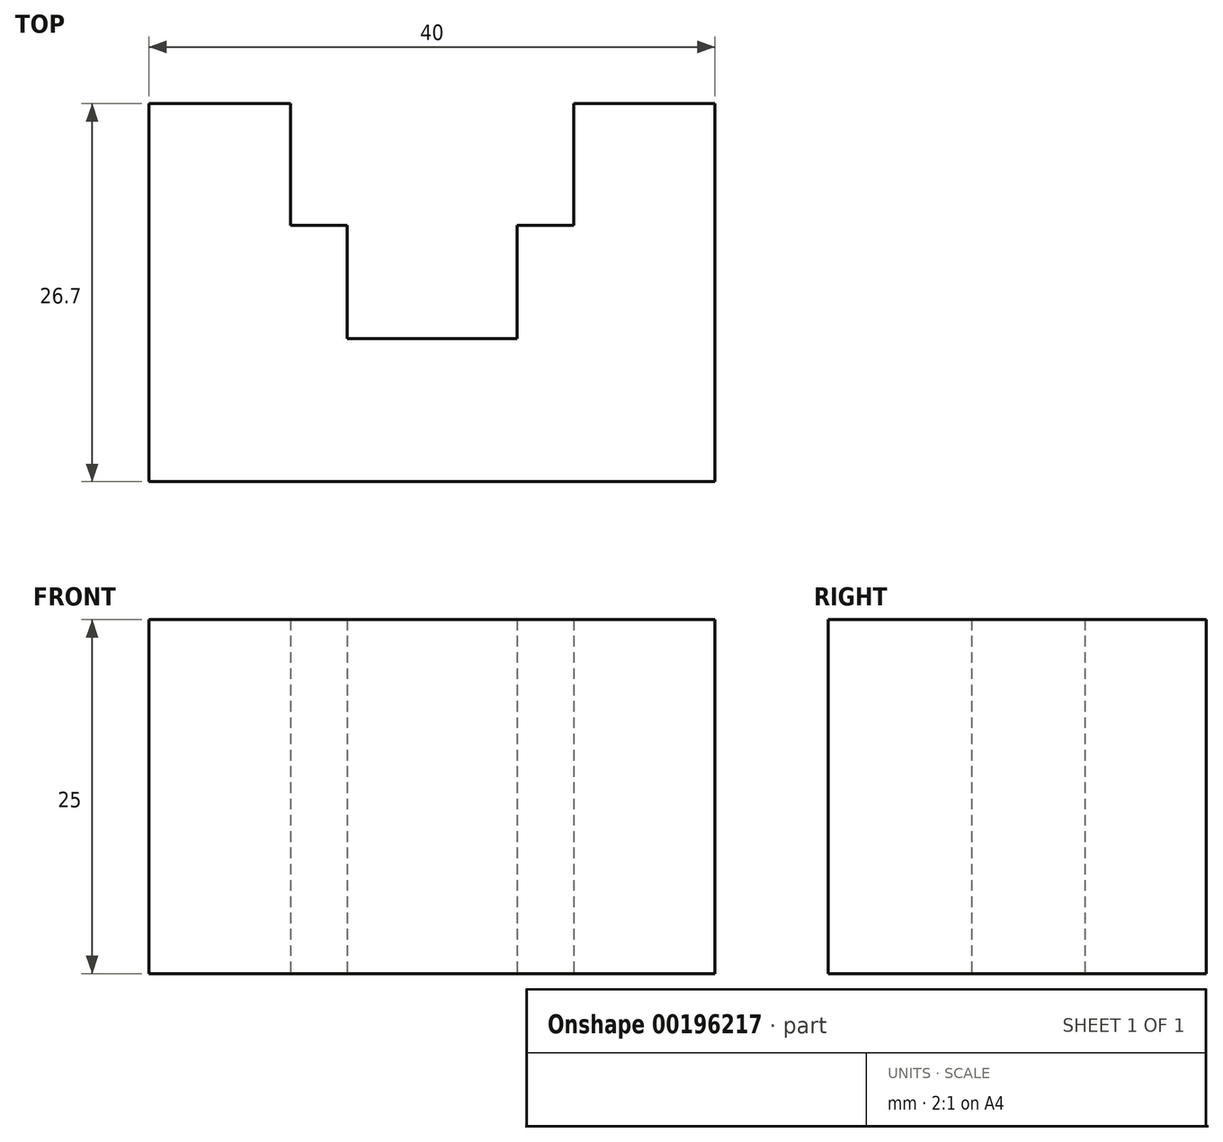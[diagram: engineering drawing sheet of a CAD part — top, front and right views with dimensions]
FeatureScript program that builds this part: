
annotation { "Feature Type Name" : "Feature", "Feature Type Description" : "" }
export const myFeature = defineFeature(function(context is Context, id is Id, definition is map)
    precondition{}
    {
        {
            var Q0;
            Q0=qCreatedBy(makeId("Top.planeOp"),FACE);
            var sketch = newSketch(context, id + "F0", { "sketchPlane" : qUnion([Q0])});
            skLineSegment(sketch, "E0", {"start": v(0, 0) * mm, "end": v(40, 0) * mm});
            skLineSegment(sketch, "E1", {"start": v(40, 0) * mm, "end": v(40, 26.7) * mm});
            skLineSegment(sketch, "E2", {"start": v(40, 26.7) * mm, "end": v(30, 26.7) * mm});
            skLineSegment(sketch, "E3", {"start": v(30, 26.7) * mm, "end": v(30, 18.1) * mm});
            skLineSegment(sketch, "E4", {"start": v(30, 18.1) * mm, "end": v(26, 18.1) * mm});
            skLineSegment(sketch, "E5", {"start": v(26, 18.1) * mm, "end": v(26, 10.1) * mm});
            skLineSegment(sketch, "E6", {"start": v(26, 10.1) * mm, "end": v(14, 10.1) * mm});
            skLineSegment(sketch, "E7", {"start": v(14, 10.1) * mm, "end": v(14, 18.1) * mm});
            skLineSegment(sketch, "E8", {"start": v(14, 18.1) * mm, "end": v(10, 18.1) * mm});
            skLineSegment(sketch, "E9", {"start": v(10, 18.1) * mm, "end": v(10, 26.7) * mm});
            skLineSegment(sketch, "E10", {"start": v(10, 26.7) * mm, "end": v(0, 26.7) * mm});
            skLineSegment(sketch, "E11", {"start": v(0, 26.7) * mm, "end": v(0, 0) * mm});
            skSolve(sketch);
        }
        {
            var Q0;
            Q0 = qSketchRegion(id + "F0", true);
            extrude(context, id + "F1", {"entities" : qUnion([Q0]), "depth" : 25 * mm});
        }
    });
